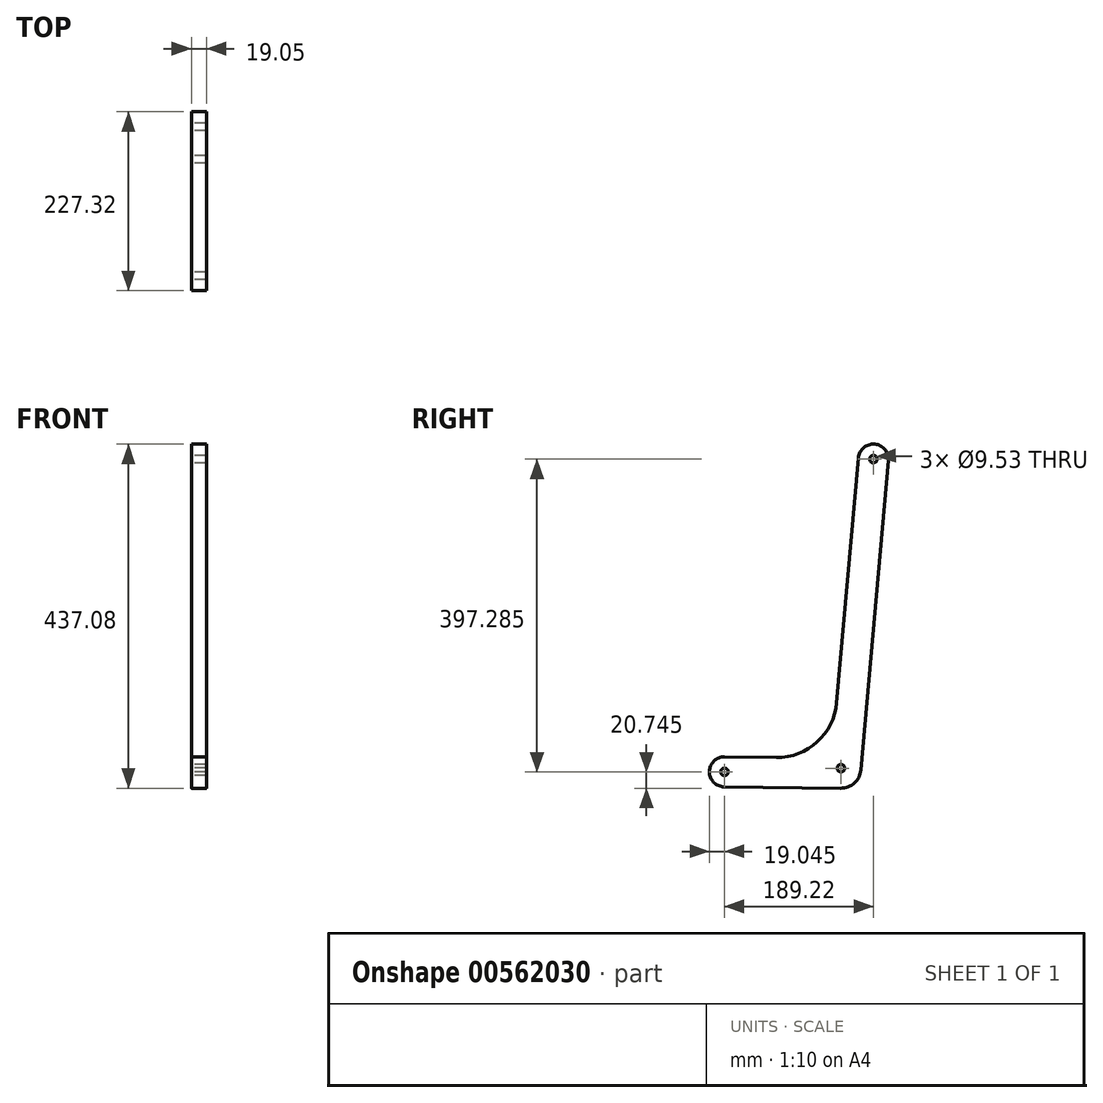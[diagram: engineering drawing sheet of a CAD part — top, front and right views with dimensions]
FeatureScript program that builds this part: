
annotation { "Feature Type Name" : "Feature", "Feature Type Description" : "" }
export const myFeature = defineFeature(function(context is Context, id is Id, definition is map)
    precondition{}
    {
        {
            var Q0;
            Q0=qCreatedBy(makeId("Right.planeOp"),FACE);
            var sketch = newSketch(context, id + "F0", { "sketchPlane" : qUnion([Q0])});
            skLineSegment(sketch, "E0", {"start": v(-513.86, 319.86) * mm, "end": v(-513.86, 78.56) * mm});
            skSolve(sketch);
        }
        {
            var Q0;
            Q0=qCreatedBy(makeId("Right.planeOp"),FACE);
            var sketch = newSketch(context, id + "F1", { "sketchPlane" : qUnion([Q0])});
            skLineSegment(sketch, "E1", {"start": v(-749.76, 256.37) * mm, "end": v(-601.81, 261.03) * mm});
            skLineSegment(sketch, "E2", {"start": v(-560.54, 653.66) * mm, "end": v(-601.81, 261.03) * mm});
            skLineSegment(sketch, "E3", {"start": v(-560.54, 653.66) * mm, "end": v(-749.76, 256.37) * mm});
            skLineSegment(sketch, "E4", {"start": v(-712.77, 291.22) * mm, "end": v(-723.7, 436.42) * mm});
            skLineSegment(sketch, "E5", {"start": v(-712.77, 291.22) * mm, "end": v(-826.16, 542.64) * mm});
            skLineSegment(sketch, "E6", {"start": v(-723.7, 436.42) * mm, "end": v(-826.16, 542.64) * mm});
            skLineSegment(sketch, "E7", {"start": v(-1007.93, 660.27) * mm, "end": v(-826.16, 542.64) * mm});
            skLineSegment(sketch, "E8", {"start": v(-1037.12, 677.37) * mm, "end": v(-1007.93, 660.27) * mm});
            skLineSegment(sketch, "E9", {"start": v(-1037.12, 677.37) * mm, "end": v(-712.77, 291.22) * mm});
            skLineSegment(sketch, "E10", {"start": v(-1007.93, 660.27) * mm, "end": v(-712.77, 291.22) * mm});
            skLineSegment(sketch, "E11", {"start": v(-601.81, 261.03) * mm, "end": v(-595.01, 401.75) * mm});
            skLineSegment(sketch, "E12", {"start": v(-601.81, 261.03) * mm, "end": v(-607.25, 655.88) * mm});
            skLineSegment(sketch, "E13", {"start": v(-595.01, 401.75) * mm, "end": v(-607.25, 655.88) * mm});
            skLineSegment(sketch, "E14", {"start": v(-723.7, 436.42) * mm, "end": v(-595.01, 401.75) * mm});
            skLineSegment(sketch, "E15", {"start": v(-826.16, 542.64) * mm, "end": v(-774.61, 590.25) * mm});
            skLineSegment(sketch, "E16", {"start": v(-749.76, 256.37) * mm, "end": v(-774.61, 590.25) * mm});
            skLineSegment(sketch, "E17", {"start": v(-1041.29, 793.41) * mm, "end": v(-774.61, 590.25) * mm});
            skLineSegment(sketch, "E18", {"start": v(-1390.78, 317.95) * mm, "end": v(-1336.8, 360.93) * mm});
            skLineSegment(sketch, "E19", {"start": v(-1336.8, 360.93) * mm, "end": v(-1295.1, 301.57) * mm});
            skLineSegment(sketch, "E20", {"start": v(-1041.29, 793.41) * mm, "end": v(-1295.1, 301.57) * mm});
            skLineSegment(sketch, "E21", {"start": v(-1295.1, 301.57) * mm, "end": v(-1037.12, 677.37) * mm});
            skLineSegment(sketch, "E22", {"start": v(-1037.12, 677.37) * mm, "end": v(-1041.29, 793.41) * mm});
            skLineSegment(sketch, "E23", {"start": v(-1007.93, 660.27) * mm, "end": v(-1336.8, 360.93) * mm});
            skLineSegment(sketch, "E24", {"start": v(-1390.78, 317.95) * mm, "end": v(-1295.1, 301.57) * mm});
            skLineSegment(sketch, "E25", {"start": v(-1295.1, 301.57) * mm, "end": v(-1295.1, 192.57) * mm});
            skLineSegment(sketch, "E26", {"start": v(-1295.1, 192.57) * mm, "end": v(-1403.22, 211.07) * mm});
            skLineSegment(sketch, "E27", {"start": v(-1403.22, 211.07) * mm, "end": v(-1390.78, 317.95) * mm});
            skLineSegment(sketch, "E28", {"start": v(-1390.78, 317.95) * mm, "end": v(-1295.1, 192.57) * mm});
            skLineSegment(sketch, "E29", {"start": v(0, 0) * mm, "end": v(0, 674.17) * mm});
            skLineSegment(sketch, "E30", {"start": v(-316.61, 320.6) * mm, "end": v(-316.61, 307.94) * mm});
            skLineSegment(sketch, "E31", {"start": v(-400.45, 218.07) * mm, "end": v(-378.01, 218.07) * mm});
            skLineSegment(sketch, "E32", {"start": v(-472.6, 74.76) * mm, "end": v(-472.6, 54.94) * mm});
            skSolve(sketch);
        }
        {
            var Q0;
            Q0=qCreatedBy(makeId("Right.planeOp"),FACE);
            var sketch = newSketch(context, id + "F2", { "sketchPlane" : qUnion([Q0])});
            skArc(sketch, "E33", {"start": v(-749.98, 237.33) * mm, "mid": v(-768.81, 256.6) * mm, "end": v(-749.55, 275.42) * mm});
            skArc(sketch, "E34", {"start": v(-579.52, 655.35) * mm, "mid": v(-558.86, 672.63) * mm, "end": v(-541.57, 651.97) * mm});
            skLineSegment(sketch, "E35", {"start": v(-749.55, 275.42) * mm, "end": v(-683.95, 274.67) * mm});
            skLineSegment(sketch, "E36", {"start": v(-607.18, 344.12) * mm, "end": v(-579.52, 655.35) * mm});
            skLineSegment(sketch, "E37", {"start": v(-541.57, 651.97) * mm, "end": v(-576.51, 258.78) * mm});
            skLineSegment(sketch, "E38", {"start": v(-749.98, 237.33) * mm, "end": v(-602.1, 235.63) * mm});
            skPoint(sketch, "E39.visualSharp", {"position": v(-578.6, 235.36) * mm});
            skArc(sketch, "E39.filletArc", {"start": v(-602.1, 235.63) * mm, "mid": v(-584.77, 242.2) * mm, "end": v(-576.51, 258.78) * mm});
            skPoint(sketch, "E40.visualSharp", {"position": v(-613.42, 273.86) * mm});
            skArc(sketch, "E40.filletArc", {"start": v(-683.95, 274.67) * mm, "mid": v(-631.96, 294.36) * mm, "end": v(-607.18, 344.12) * mm});
            skCircle(sketch, "E41", {"center": v(-749.76, 256.37) * mm, "radius": 4.76 * mm});
            skCircle(sketch, "E42", {"center": v(-601.81, 261.03) * mm, "radius": 4.76 * mm});
            skCircle(sketch, "E43", {"center": v(-560.54, 653.66) * mm, "radius": 4.76 * mm});
            skSolve(sketch);
        }
        {
            var Q0;
            Q0 = qSketchRegion(id + "F2", true);
            extrude(context, id + "F3", {"entities" : qUnion([Q0]), "depth" : 19.05 * mm, "offsetDistance" : 25.4 * mm});
        }
    });
